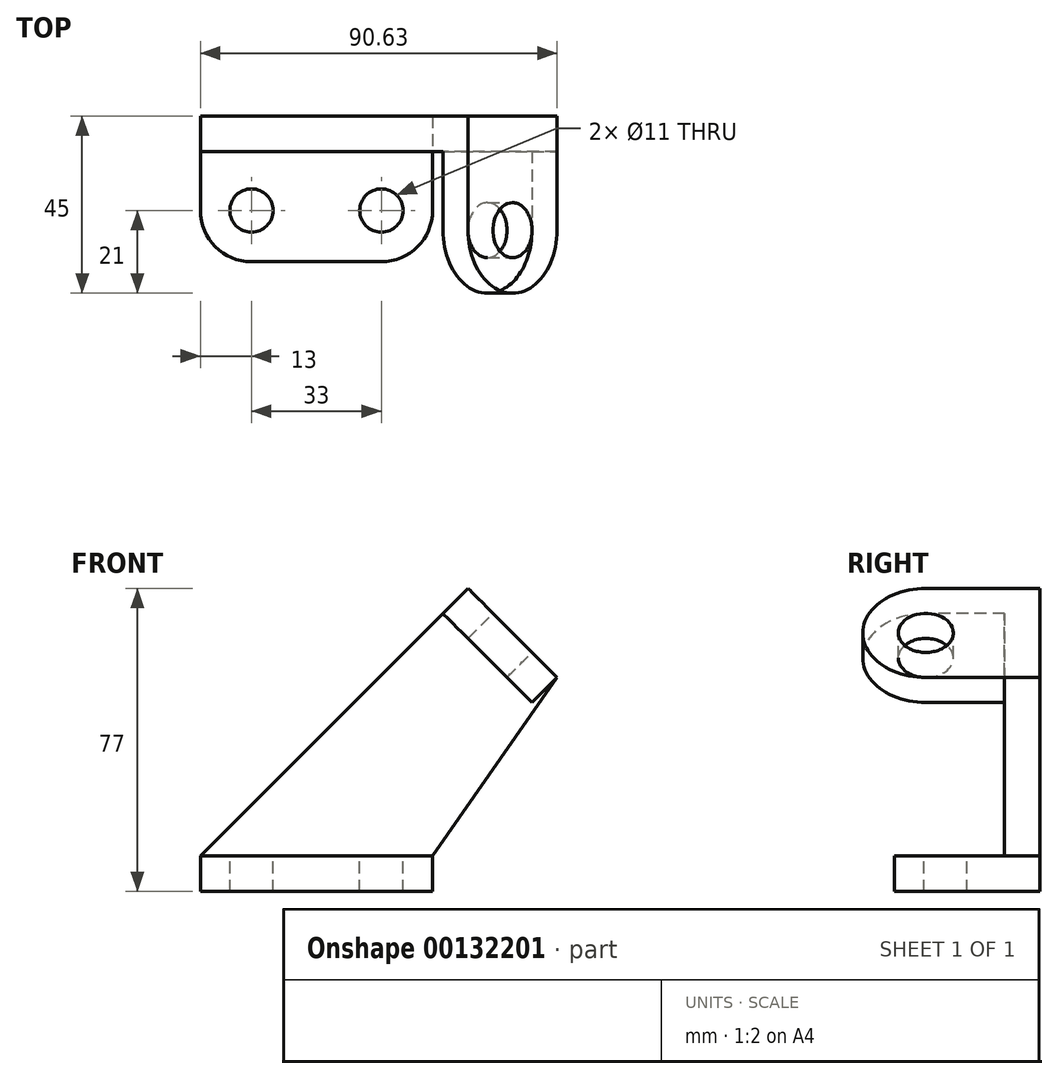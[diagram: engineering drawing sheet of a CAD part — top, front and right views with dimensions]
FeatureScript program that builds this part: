
annotation { "Feature Type Name" : "Feature", "Feature Type Description" : "" }
export const myFeature = defineFeature(function(context is Context, id is Id, definition is map)
    precondition{}
    {
        {
            var Q0;
            Q0=qCreatedBy(makeId("Top.planeOp"),FACE);
            var sketch = newSketch(context, id + "F0", { "sketchPlane" : qUnion([Q0])});
            skLineSegment(sketch, "E0.bottom", {"start": v(0, 0) * mm, "end": v(59, 0) * mm});
            skLineSegment(sketch, "E0.top", {"start": v(13, -28) * mm, "end": v(46, -28) * mm});
            skLineSegment(sketch, "E0.left", {"start": v(0, 0) * mm, "end": v(0, -15) * mm});
            skLineSegment(sketch, "E0.right", {"start": v(59, 0) * mm, "end": v(59, -15) * mm});
            skPoint(sketch, "E1.visualSharp", {"position": v(0, -28) * mm});
            skArc(sketch, "E1.filletArc", {"start": v(0, -15) * mm, "mid": v(3.8, -24.2) * mm, "end": v(13, -28) * mm});
            skPoint(sketch, "E2.visualSharp", {"position": v(59, -28) * mm});
            skArc(sketch, "E2.filletArc", {"start": v(46, -28) * mm, "mid": v(55.2, -24.2) * mm, "end": v(59, -15) * mm});
            skCircle(sketch, "E3", {"center": v(13, -15) * mm, "radius": 5.5 * mm});
            skCircle(sketch, "E4", {"center": v(46, -15) * mm, "radius": 5.5 * mm});
            skSolve(sketch);
        }
        {
            var Q0;
            Q0=makeQuery(id+"F0.imprint","IMPRINT",FACE,{"disambiguationData":[TD([[makeQuery(id+"F0.imprint","IMPRINT",EDGE,{"derivedFrom":sQuery(id+"F0.wireOp",EDGE,"E0.bottom")}),-1.0]])]});
            extrude(context, id + "F1", {"entities" : qUnion([Q0]), "oppositeDirection" : true, "depth" : 9 * mm});
        }
        {
            var Q0;
            Q0=makeQuery(id+"F1.opExtrude","SWEPT_FACE",FACE,{"disambiguationData":[OSD([sQuery(id+"F0.wireOp",EDGE,"E0.bottom")])]});
            var sketch = newSketch(context, id + "F2", { "sketchPlane" : qUnion([Q0])});
            skLineSegment(sketch, "E5", {"start": v(-72, -19.9) * mm, "end": v(-72, 64) * mm, "construction": true});
            skLineSegment(sketch, "E6", {"start": v(-120, 64) * mm, "end": v(49.22, 64) * mm, "construction": true});
            skLineSegment(sketch, "E7", {"start": v(-68, 68) * mm, "end": v(-90.63, 45.37) * mm});
            skLineSegment(sketch, "E8", {"start": v(-90.63, 45.37) * mm, "end": v(-59, 0) * mm});
            skLineSegment(sketch, "E9", {"start": v(-59, 0) * mm, "end": v(0, 0) * mm});
            skLineSegment(sketch, "E10", {"start": v(0, 0) * mm, "end": v(-68, 68) * mm});
            skLineSegment(sketch, "E11.0", {"start": v(-59, -9) * mm, "end": v(-59, 0) * mm});
            skLineSegment(sketch, "E12.0", {"start": v(0, -9) * mm, "end": v(-59, -9) * mm});
            skLineSegment(sketch, "E13.0", {"start": v(0, -9) * mm, "end": v(0, 0) * mm});
            skSolve(sketch);
        }
        {
            var Q0;
            Q0=makeQuery(id+"F2.imprint","IMPRINT",FACE,{"disambiguationData":[TD([[makeQuery(id+"F2.imprint","IMPRINT",EDGE,{"derivedFrom":sQuery(id+"F2.wireOp",EDGE,"E9")}),1.0]])]});
            var Q1;
            Q1=makeQuery(id+"F2.imprint","IMPRINT",FACE,{"disambiguationData":[TD([[makeQuery(id+"F2.imprint","IMPRINT",EDGE,{"derivedFrom":sQuery(id+"F2.wireOp",EDGE,"E7")}),1.0]])]});
            extrude(context, id + "F3", {"entities" : qUnion([Q0, Q1]), "operationType" : NewBodyOperationType.ADD, "depth" : 9 * mm});
        }
        {
            var Q0;
            Q0=makeQuery(id+"F3.opExtrude","SWEPT_FACE",FACE,{"disambiguationData":[OSD([sQuery(id+"F2.wireOp",EDGE,"E7")])]});
            var sketch = newSketch(context, id + "F4", { "sketchPlane" : qUnion([Q0])});
            skLineSegment(sketch, "E14.bottom", {"start": v(9, 0) * mm, "end": v(-20, 0) * mm});
            skLineSegment(sketch, "E14.top", {"start": v(9, -32) * mm, "end": v(-20, -32) * mm});
            skLineSegment(sketch, "E14.left", {"start": v(9, 0) * mm, "end": v(9, -32) * mm});
            skLineSegment(sketch, "E14.right", {"start": v(-20, 0) * mm, "end": v(-20, -32) * mm});
            skArc(sketch, "E15", {"start": v(-20, 0) * mm, "mid": v(-36, -16) * mm, "end": v(-20, -32) * mm});
            skCircle(sketch, "E16", {"center": v(-20, -16) * mm, "radius": 7 * mm});
            skLineSegment(sketch, "E17", {"start": v(0, 0) * mm, "end": v(0, -32) * mm});
            skSolve(sketch);
        }
        {
            var Q0;
            {var subQ9=sQuery(id+"F4.wireOp",EDGE,"E17");Q0=makeQuery(id+"F4.imprint","IMPRINT",FACE,{"disambiguationData":[TD([[makeQuery(id+"F4.imprint","IMPRINT",EDGE,{"derivedFrom":subQ9}),-1.0]])]});}
            var Q1;
            {var subQ0=sQuery(id+"F4.wireOp",EDGE,"E15");Q1=makeQuery(id+"F4.imprint","IMPRINT",FACE,{"disambiguationData":[TD([[makeQuery(id+"F4.imprint","IMPRINT",EDGE,{"derivedFrom":subQ0}),1.0]])]});}
            extrude(context, id + "F5", {"entities" : qUnion([Q0, Q1]), "operationType" : NewBodyOperationType.ADD, "oppositeDirection" : true, "depth" : 9 * mm});
        }
    });
